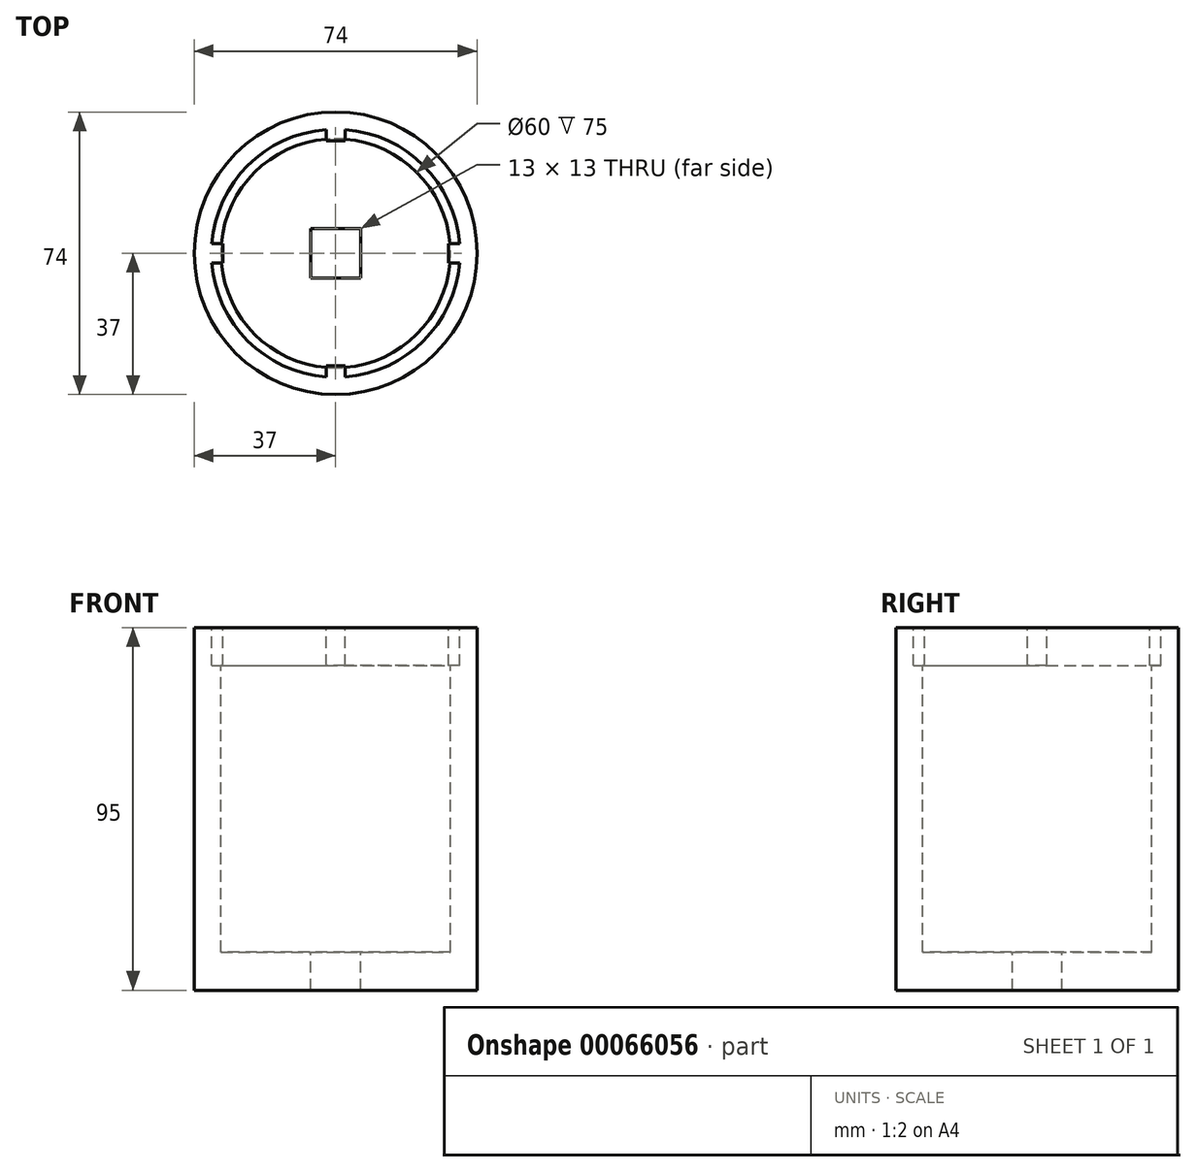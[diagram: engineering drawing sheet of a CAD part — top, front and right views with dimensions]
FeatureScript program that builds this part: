
annotation { "Feature Type Name" : "Feature", "Feature Type Description" : "" }
export const myFeature = defineFeature(function(context is Context, id is Id, definition is map)
    precondition{}
    {
        {
            var Q0;
            Q0=qCreatedBy(makeId("Top.planeOp"),FACE);
            var sketch = newSketch(context, id + "F0", { "sketchPlane" : qUnion([Q0])});
            skCircle(sketch, "E0", {"center": v(0, 0) * mm, "radius": 37 * mm});
            skCircle(sketch, "E1", {"center": v(0, 0) * mm, "radius": 32.5 * mm});
            skLineSegment(sketch, "E2.bottom", {"start": v(-32.5, 2.5) * mm, "end": v(-29.5, 2.5) * mm});
            skLineSegment(sketch, "E2.top", {"start": v(-32.5, -2.5) * mm, "end": v(-29.5, -2.5) * mm});
            skLineSegment(sketch, "E2.right", {"start": v(-29.5, 2.5) * mm, "end": v(-29.5, -2.5) * mm});
            skLineSegment(sketch, "E3.1.0", {"start": v(-2.5, -32.5) * mm, "end": v(-2.5, -29.5) * mm});
            skLineSegment(sketch, "E3.1.1", {"start": v(-2.5, -29.5) * mm, "end": v(2.5, -29.5) * mm});
            skLineSegment(sketch, "E3.1.2", {"start": v(2.5, -32.5) * mm, "end": v(2.5, -29.5) * mm});
            skLineSegment(sketch, "E3.2.0", {"start": v(32.5, -2.5) * mm, "end": v(29.5, -2.5) * mm});
            skLineSegment(sketch, "E3.2.1", {"start": v(29.5, -2.5) * mm, "end": v(29.5, 2.5) * mm});
            skLineSegment(sketch, "E3.2.2", {"start": v(32.5, 2.5) * mm, "end": v(29.5, 2.5) * mm});
            skLineSegment(sketch, "E3.3.0", {"start": v(2.5, 32.5) * mm, "end": v(2.5, 29.5) * mm});
            skLineSegment(sketch, "E3.3.1", {"start": v(2.5, 29.5) * mm, "end": v(-2.5, 29.5) * mm});
            skLineSegment(sketch, "E3.3.2", {"start": v(-2.5, 32.5) * mm, "end": v(-2.5, 29.5) * mm});
            skSolve(sketch);
        }
        {
            var Q0;
            Q0=makeQuery(id+"F0.imprint","IMPRINT",FACE,{"disambiguationData":[TD([[makeQuery(id+"F0.imprint","IMPRINT",EDGE,{"derivedFrom":sQuery(id+"F0.wireOp",EDGE,"E0")}),1.0]])]});
            var Q1;
            {var subQ0=sQuery(id+"F0.wireOp",EDGE,"E3.3.1");Q1=makeQuery(id+"F0.imprint","IMPRINT",FACE,{"disambiguationData":[TD([[makeQuery(id+"F0.imprint","IMPRINT",EDGE,{"derivedFrom":subQ0}),-1.0]])]});}
            var Q2;
            {var subQ3=sQuery(id+"F0.wireOp",EDGE,"E3.2.1");Q2=makeQuery(id+"F0.imprint","IMPRINT",FACE,{"disambiguationData":[TD([[makeQuery(id+"F0.imprint","IMPRINT",EDGE,{"derivedFrom":subQ3}),-1.0]])]});}
            var Q3;
            {var subQ3=sQuery(id+"F0.wireOp",EDGE,"E3.1.1");Q3=makeQuery(id+"F0.imprint","IMPRINT",FACE,{"disambiguationData":[TD([[makeQuery(id+"F0.imprint","IMPRINT",EDGE,{"derivedFrom":subQ3}),-1.0]])]});}
            var Q4;
            {var subQ0=sQuery(id+"F0.wireOp",EDGE,"E2.right");Q4=makeQuery(id+"F0.imprint","IMPRINT",FACE,{"disambiguationData":[TD([[makeQuery(id+"F0.imprint","IMPRINT",EDGE,{"derivedFrom":subQ0}),-1.0]])]});}
            extrude(context, id + "F1", {"entities" : qUnion([Q0, Q1, Q2, Q3, Q4]), "oppositeDirection" : true, "depth" : 10 * mm});
        }
        {
            var Q0;
            Q0=makeQuery(id+"F1.opExtrude","CAP_FACE",FACE,{"disambiguationData":[OSD([sQuery(id+"F0.wireOp",EDGE,"E0"),sQuery(id+"F0.wireOp",EDGE,"E1"),sQuery(id+"F0.wireOp",EDGE,"E2.bottom"),sQuery(id+"F0.wireOp",EDGE,"E2.top"),sQuery(id+"F0.wireOp",EDGE,"E2.right"),sQuery(id+"F0.wireOp",EDGE,"E3.1.0"),sQuery(id+"F0.wireOp",EDGE,"E3.1.1"),sQuery(id+"F0.wireOp",EDGE,"E3.1.2"),sQuery(id+"F0.wireOp",EDGE,"E3.2.0"),sQuery(id+"F0.wireOp",EDGE,"E3.2.1"),sQuery(id+"F0.wireOp",EDGE,"E3.2.2"),sQuery(id+"F0.wireOp",EDGE,"E3.3.0"),sQuery(id+"F0.wireOp",EDGE,"E3.3.1"),sQuery(id+"F0.wireOp",EDGE,"E3.3.2")])],"isStart":false});
            var sketch = newSketch(context, id + "F2", { "sketchPlane" : qUnion([Q0])});
            skCircle(sketch, "E4", {"center": v(0, 0) * mm, "radius": 30 * mm});
            skCircle(sketch, "E5", {"center": v(0, 0) * mm, "radius": 37 * mm});
            skSolve(sketch);
        }
        {
            var Q0;
            {var subQ0=sQuery(id+"F0.wireOp",EDGE,"E3.3.0");var subQ4=sQuery(id+"F0.wireOp",EDGE,"E1");var subQ6=makeQuery(id+"F1.opExtrude","CAP_EDGE",EDGE,{"disambiguationData":[OSD([subQ4]),TDD([makeQuery(id+"F0.imprint","IMPRINT",EDGE,{"disambiguationData":[TD([[makeQuery(id+"F0.imprint","INTERSECT",VERTEX,{"derivedFrom":[subQ4,subQ0]}),1.0]])],"derivedFrom":subQ4})])],"isStart":false});Q0=makeQuery(id+"F2.imprint","IMPRINT",FACE,{"disambiguationData":[TD([[makeQuery(id+"F2.imprint","IMPRINT",EDGE,{"derivedFrom":subQ6}),-1.0]])]});}
            var Q1;
            Q1=makeQuery(id+"F2.imprint","IMPRINT",FACE,{"disambiguationData":[TD([[makeQuery(id+"F2.imprint","IMPRINT",EDGE,{"derivedFrom":sQuery(id+"F2.wireOp",EDGE,"E5")}),-1.0]])]});
            var Q2;
            {var subQ0=sQuery(id+"F0.wireOp",EDGE,"E3.3.2");var subQ4=sQuery(id+"F0.wireOp",EDGE,"E1");var subQ6=makeQuery(id+"F1.opExtrude","CAP_EDGE",EDGE,{"disambiguationData":[OSD([subQ4]),TDD([makeQuery(id+"F0.imprint","IMPRINT",EDGE,{"disambiguationData":[TD([[makeQuery(id+"F0.imprint","INTERSECT",VERTEX,{"derivedFrom":[subQ4,subQ0]}),-1.0]])],"derivedFrom":subQ4})])],"isStart":false});Q2=makeQuery(id+"F2.imprint","IMPRINT",FACE,{"disambiguationData":[TD([[makeQuery(id+"F2.imprint","IMPRINT",EDGE,{"derivedFrom":subQ6}),-1.0]])]});}
            var Q3;
            {var subQ4=sQuery(id+"F0.wireOp",EDGE,"E1");var subQ5=sQuery(id+"F0.wireOp",EDGE,"E2.top");var subQ6=makeQuery(id+"F1.opExtrude","CAP_EDGE",EDGE,{"disambiguationData":[OSD([subQ4]),TDD([makeQuery(id+"F0.imprint","IMPRINT",EDGE,{"disambiguationData":[TD([[makeQuery(id+"F0.imprint","INTERSECT",VERTEX,{"derivedFrom":[subQ4,subQ5]}),-1.0]])],"derivedFrom":subQ4})])],"isStart":false});Q3=makeQuery(id+"F2.imprint","IMPRINT",FACE,{"disambiguationData":[TD([[makeQuery(id+"F2.imprint","IMPRINT",EDGE,{"derivedFrom":subQ6}),-1.0]])]});}
            var Q4;
            {var subQ4=sQuery(id+"F0.wireOp",EDGE,"E1");var subQ5=sQuery(id+"F0.wireOp",EDGE,"E3.1.2");var subQ6=makeQuery(id+"F1.opExtrude","CAP_EDGE",EDGE,{"disambiguationData":[OSD([subQ4]),TDD([makeQuery(id+"F0.imprint","IMPRINT",EDGE,{"disambiguationData":[TD([[makeQuery(id+"F0.imprint","INTERSECT",VERTEX,{"derivedFrom":[subQ4,subQ5]}),-1.0]])],"derivedFrom":subQ4})])],"isStart":false});Q4=makeQuery(id+"F2.imprint","IMPRINT",FACE,{"disambiguationData":[TD([[makeQuery(id+"F2.imprint","IMPRINT",EDGE,{"derivedFrom":subQ6}),-1.0]])]});}
            extrude(context, id + "F3", {"entities" : qUnion([Q0, Q1, Q2, Q3, Q4]), "operationType" : NewBodyOperationType.ADD, "depth" : 75 * mm});
        }
        {
            var Q0;
            Q0=makeQuery(id+"F3.opExtrude","CAP_FACE",FACE,{"disambiguationData":[OSD([sQuery(id+"F2.wireOp",EDGE,"E4"),sQuery(id+"F2.wireOp",EDGE,"E5")])],"isStart":false});
            var sketch = newSketch(context, id + "F4", { "sketchPlane" : qUnion([Q0])});
            skCircle(sketch, "E6", {"center": v(0, 0) * mm, "radius": 37 * mm});
            skLineSegment(sketch, "E7", {"start": v(-21.6, 0) * mm, "end": v(22.85, 0) * mm, "construction": true});
            skLineSegment(sketch, "E8", {"start": v(0, 17.47) * mm, "end": v(0, -17.05) * mm, "construction": true});
            skLineSegment(sketch, "E9.rect.bottom", {"start": v(-6.5, -6.5) * mm, "end": v(6.5, -6.5) * mm});
            skLineSegment(sketch, "E9.rect.top", {"start": v(-6.5, 6.5) * mm, "end": v(6.5, 6.5) * mm});
            skLineSegment(sketch, "E9.rect.left", {"start": v(-6.5, -6.5) * mm, "end": v(-6.5, 6.5) * mm});
            skLineSegment(sketch, "E9.rect.right", {"start": v(6.5, -6.5) * mm, "end": v(6.5, 6.5) * mm});
            skSolve(sketch);
        }
        {
            var Q0;
            Q0=makeQuery(id+"F4.imprint","IMPRINT",FACE,{"disambiguationData":[TD([[makeQuery(id+"F4.imprint","IMPRINT",EDGE,{"derivedFrom":sQuery(id+"F4.wireOp",EDGE,"E9.rect.bottom")}),-1.0]])]});
            var Q1;
            Q1=makeQuery(id+"F4.imprint","IMPRINT",FACE,{"disambiguationData":[TD([[makeQuery(id+"F4.imprint","IMPRINT",EDGE,{"derivedFrom":sQuery(id+"F4.wireOp",EDGE,"E6")}),-1.0]])]});
            extrude(context, id + "F5", {"entities" : qUnion([Q0, Q1]), "operationType" : NewBodyOperationType.ADD, "depth" : 10 * mm});
        }
    });
